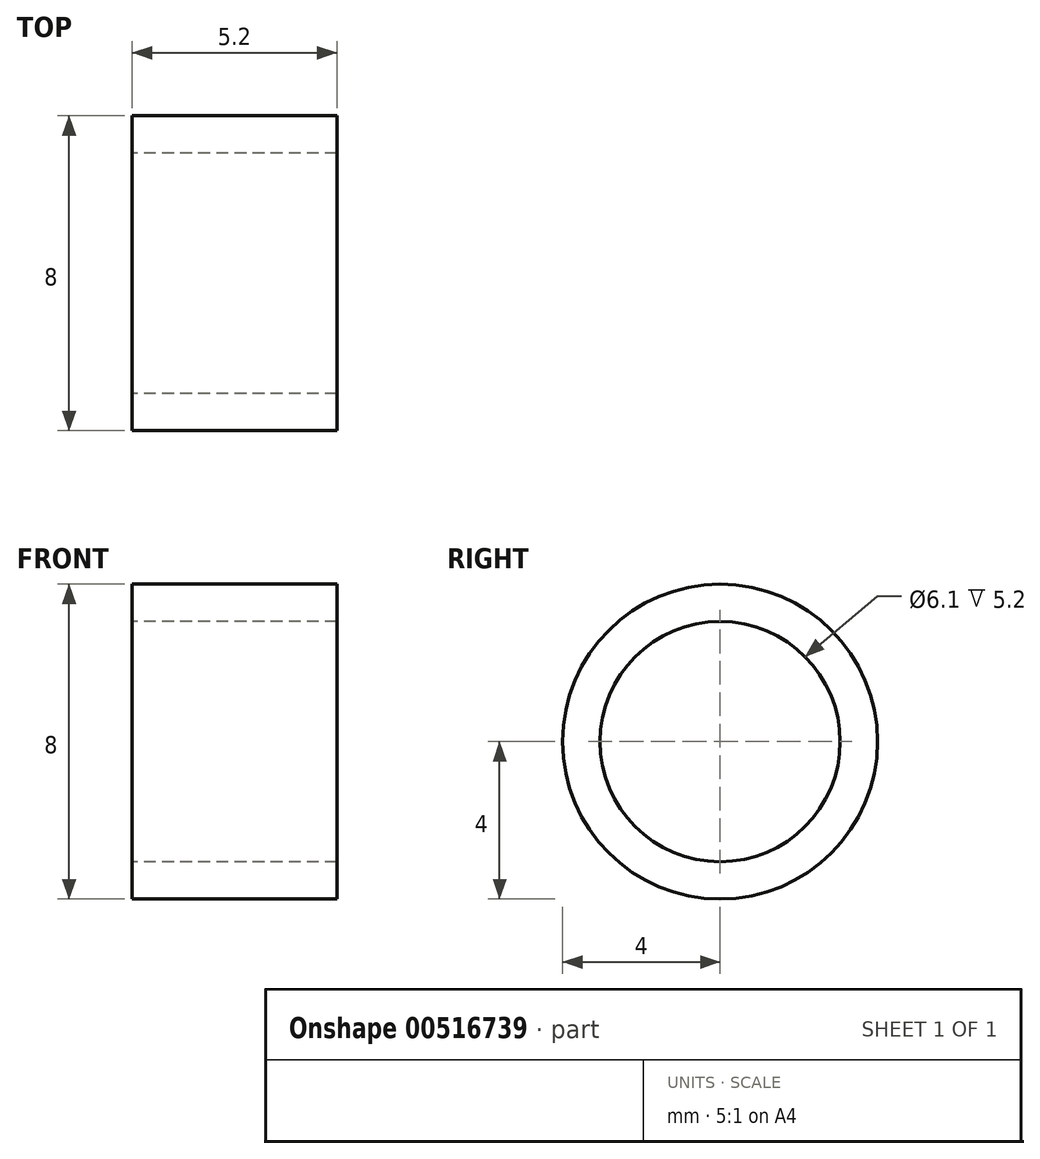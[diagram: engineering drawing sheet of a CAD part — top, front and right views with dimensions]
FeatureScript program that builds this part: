
annotation { "Feature Type Name" : "Feature", "Feature Type Description" : "" }
export const myFeature = defineFeature(function(context is Context, id is Id, definition is map)
    precondition{}
    {
        {
            var Q0;
            Q0=qCreatedBy(makeId("Front.planeOp"),FACE);
            var sketch = newSketch(context, id + "F0", { "sketchPlane" : qUnion([Q0])});
            skLineSegment(sketch, "E0.bottom", {"start": v(0, 4) * mm, "end": v(5.2, 4) * mm});
            skLineSegment(sketch, "E0.top", {"start": v(0, 3.05) * mm, "end": v(5.2, 3.05) * mm});
            skLineSegment(sketch, "E0.left", {"start": v(0, 4) * mm, "end": v(0, 3.05) * mm});
            skLineSegment(sketch, "E0.right", {"start": v(5.2, 4) * mm, "end": v(5.2, 3.05) * mm});
            skLineSegment(sketch, "E1", {"start": v(-11.1, 0) * mm, "end": v(13.8, 0) * mm, "construction": true});
            skSolve(sketch);
        }
        {
            var Q0;
            Q0 = qSketchRegion(id + "F0", true);
            var Q1;
            Q1=sQuery(id+"F0.wireOp",EDGE,"E1");
            revolve(context, id + "F1", {"entities" : qUnion([Q0]), "axis" : qUnion([Q1]), "revolveType" : RevolveType.FULL});
        }
    });
